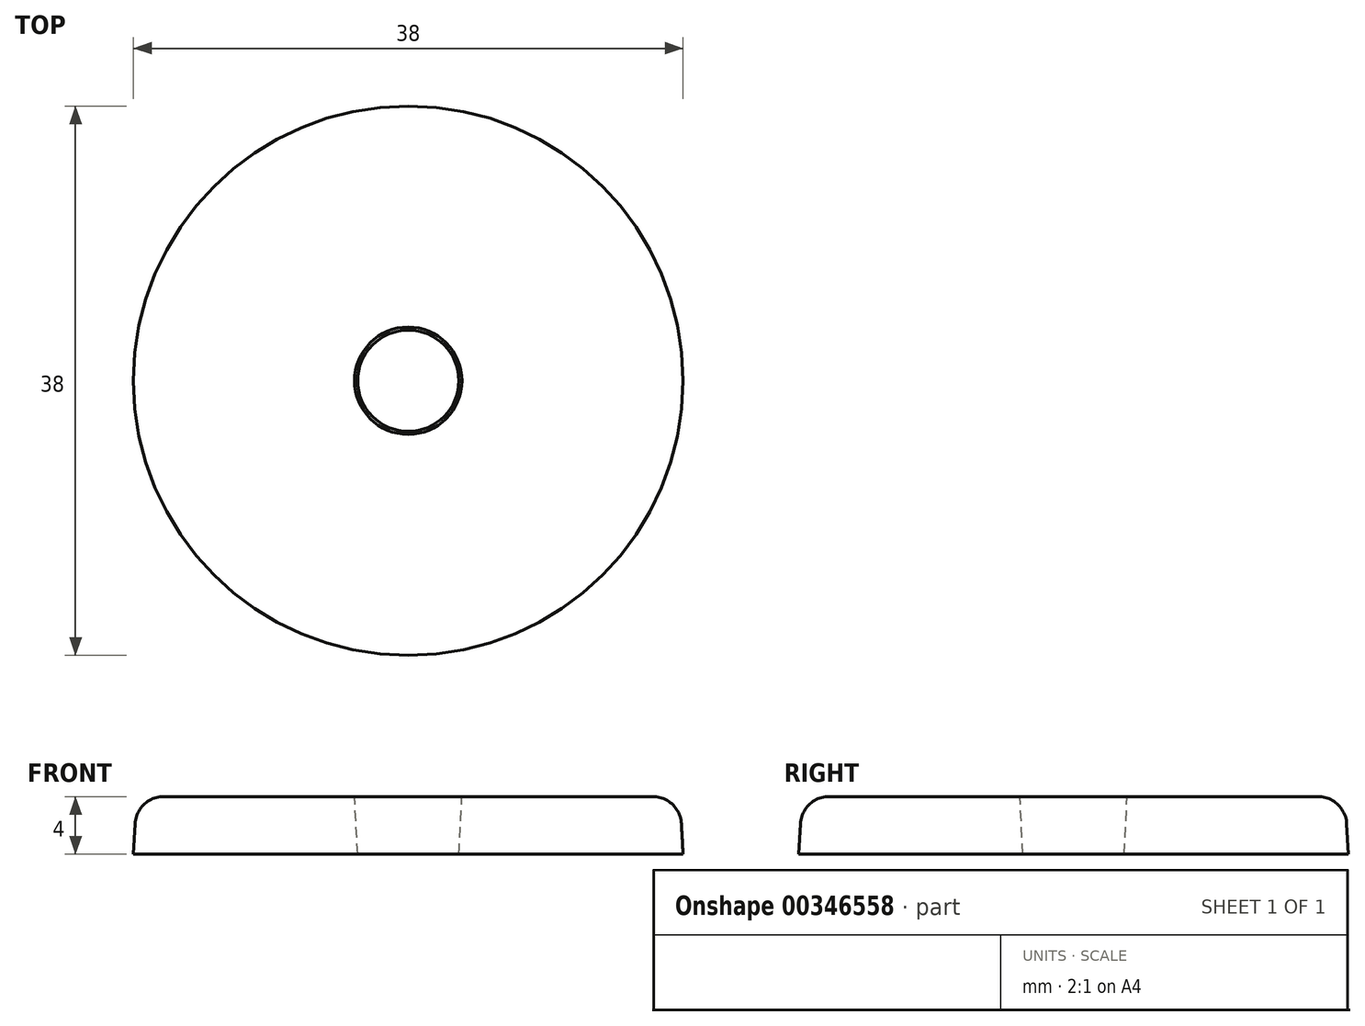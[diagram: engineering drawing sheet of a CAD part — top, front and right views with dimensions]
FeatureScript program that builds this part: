
annotation { "Feature Type Name" : "Feature", "Feature Type Description" : "" }
export const myFeature = defineFeature(function(context is Context, id is Id, definition is map)
    precondition{}
    {
        {
            var Q0;
            Q0=qCreatedBy(makeId("Top.planeOp"),FACE);
            var sketch = newSketch(context, id + "F0", { "sketchPlane" : qUnion([Q0])});
            skCircle(sketch, "E0", {"center": v(0, 0) * mm, "radius": 19 * mm});
            skCircle(sketch, "E1", {"center": v(0, 0) * mm, "radius": 3.5 * mm});
            skSolve(sketch);
        }
        {
            var Q0;
            Q0=makeQuery(id+"F0.imprint","IMPRINT",FACE,{"disambiguationData":[TD([[makeQuery(id+"F0.imprint","IMPRINT",EDGE,{"derivedFrom":sQuery(id+"F0.wireOp",EDGE,"E0")}),1.0]])]});
            extrude(context, id + "F1", {"entities" : qUnion([Q0]), "depth" : 4 * mm, "hasDraft" : true, "draftAngle" : 3 * degree, "draftPullDirection" : true});
        }
        {
            var Q0;
            Q0=makeQuery(id+"F1.opExtrude","CAP_EDGE",EDGE,{"disambiguationData":[OSD([sQuery(id+"F0.wireOp",EDGE,"E0")])],"isStart":false});
            fillet(context, id + "F2", {"entities" : qUnion([Q0]), "radius" : 2 * mm, "tangentPropagation" : true, "allowEdgeOverflow" : false});
        }
    });
